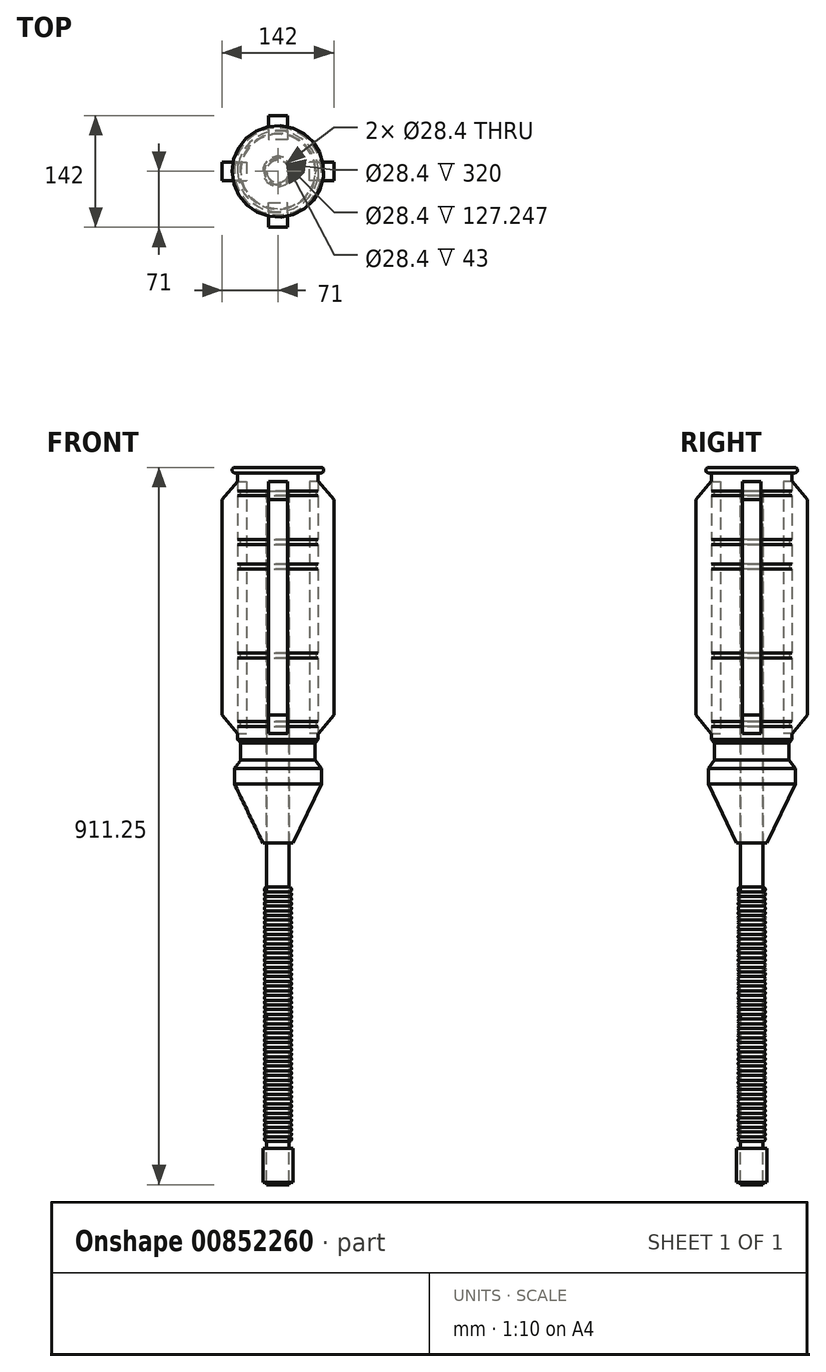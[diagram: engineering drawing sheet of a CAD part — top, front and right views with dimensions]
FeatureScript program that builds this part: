
annotation { "Feature Type Name" : "Feature", "Feature Type Description" : "" }
export const myFeature = defineFeature(function(context is Context, id is Id, definition is map)
    precondition{}
    {
        {
            var Q0;
            Q0=qCreatedBy(makeId("Front.planeOp"),FACE);
            var sketch = newSketch(context, id + "F0", { "sketchPlane" : qUnion([Q0])});
            skLineSegment(sketch, "E0", {"start": v(55.2, 58.28) * mm, "end": v(55.2, 78.28) * mm});
            skLineSegment(sketch, "E1", {"start": v(47.2, 88.53) * mm, "end": v(47.2, 110.53) * mm});
            skLineSegment(sketch, "E2", {"start": v(47.2, 110.53) * mm, "end": v(14.2, 110.53) * mm});
            skLineSegment(sketch, "E3", {"start": v(14.2, -16.72) * mm, "end": v(14.2, 110.53) * mm});
            skLineSegment(sketch, "E4", {"start": v(55.2, 78.28) * mm, "end": v(47.2, 88.53) * mm});
            skLineSegment(sketch, "E5", {"start": v(19.2, -16.72) * mm, "end": v(14.2, -16.72) * mm});
            skLineSegment(sketch, "E6", {"start": v(14.2, 110.53) * mm, "end": v(47.2, 110.53) * mm});
            skLineSegment(sketch, "E7", {"start": v(55.2, 58.28) * mm, "end": v(19.2, -16.72) * mm});
            skSolve(sketch);
        }
        {
            var Q0;
            Q0=qCreatedBy(makeId("Front.planeOp"),FACE);
            var sketch = newSketch(context, id + "F1", { "sketchPlane" : qUnion([Q0])});
            skLineSegment(sketch, "E8", {"start": v(0, 0) * mm, "end": v(0, 46.49) * mm});
            skSolve(sketch);
        }
        {
            var Q0;
            Q0 = qSketchRegion(id + "F0", true);
            var Q1;
            Q1=sQuery(id+"F1.wireOp",EDGE,"E8");
            revolve(context, id + "F2", {"surfaceOperationType" : NewSurfaceOperationType.NEW, "entities" : qUnion([Q0]), "axis" : qUnion([Q1]), "revolveType" : RevolveType.FULL});
        }
        {
            var Q0;
            Q0=qCreatedBy(makeId("Front.planeOp"),FACE);
            var sketch = newSketch(context, id + "F3", { "sketchPlane" : qUnion([Q0])});
            skLineSegment(sketch, "E9", {"start": v(51.2, 113.53) * mm, "end": v(51.2, 131.53) * mm});
            skLineSegment(sketch, "E10", {"start": v(54.74, 460.53) * mm, "end": v(14.2, 460.53) * mm});
            skLineSegment(sketch, "E11", {"start": v(51.2, 453.53) * mm, "end": v(54.7, 453.53) * mm});
            skLineSegment(sketch, "E12", {"start": v(58.2, 457.03) * mm, "end": v(58.2, 457.03) * mm});
            skLineSegment(sketch, "E13", {"start": v(54.7, 460.53) * mm, "end": v(54.74, 460.53) * mm});
            skPoint(sketch, "E14.visualSharp", {"position": v(58.2, 460.53) * mm});
            skArc(sketch, "E14.filletArc", {"start": v(58.2, 457.03) * mm, "mid": v(57.17, 459.5) * mm, "end": v(54.7, 460.53) * mm});
            skPoint(sketch, "E15.visualSharp", {"position": v(58.2, 453.53) * mm});
            skArc(sketch, "E15.filletArc", {"start": v(54.7, 453.53) * mm, "mid": v(57.17, 454.56) * mm, "end": v(58.2, 457.03) * mm});
            skLineSegment(sketch, "E16", {"start": v(51.2, 131.53) * mm, "end": v(48.2, 131.53) * mm});
            skLineSegment(sketch, "E17", {"start": v(48.2, 131.53) * mm, "end": v(48.2, 137.53) * mm});
            skLineSegment(sketch, "E18", {"start": v(48.2, 137.53) * mm, "end": v(51.2, 137.53) * mm});
            skLineSegment(sketch, "E19.trimOffspring", {"start": v(51.2, 137.53) * mm, "end": v(51.2, 218.53) * mm});
            skLineSegment(sketch, "E20", {"start": v(51.2, 218.53) * mm, "end": v(48.2, 218.53) * mm});
            skLineSegment(sketch, "E21", {"start": v(48.2, 218.53) * mm, "end": v(48.2, 224.53) * mm});
            skLineSegment(sketch, "E22", {"start": v(48.2, 224.53) * mm, "end": v(51.2, 224.53) * mm});
            skLineSegment(sketch, "E23", {"start": v(51.2, 331.53) * mm, "end": v(48.2, 331.53) * mm});
            skLineSegment(sketch, "E24", {"start": v(48.2, 331.53) * mm, "end": v(48.2, 337.53) * mm});
            skLineSegment(sketch, "E25", {"start": v(48.2, 337.53) * mm, "end": v(51.2, 337.53) * mm});
            skLineSegment(sketch, "E26", {"start": v(51.2, 362.53) * mm, "end": v(48.2, 362.53) * mm});
            skLineSegment(sketch, "E27", {"start": v(48.2, 362.53) * mm, "end": v(48.2, 368.53) * mm});
            skLineSegment(sketch, "E28", {"start": v(48.2, 368.53) * mm, "end": v(51.2, 368.53) * mm});
            skLineSegment(sketch, "E29", {"start": v(51.2, 424.53) * mm, "end": v(48.2, 424.53) * mm});
            skLineSegment(sketch, "E30", {"start": v(48.2, 424.53) * mm, "end": v(48.2, 430.53) * mm});
            skLineSegment(sketch, "E31", {"start": v(48.2, 430.53) * mm, "end": v(51.2, 430.53) * mm});
            skLineSegment(sketch, "E32.trimOffspring", {"start": v(51.2, 430.53) * mm, "end": v(51.2, 453.53) * mm});
            skLineSegment(sketch, "E33.trimOffspring", {"start": v(51.2, 368.53) * mm, "end": v(51.2, 424.53) * mm});
            skLineSegment(sketch, "E34.trimOffspring", {"start": v(51.2, 337.53) * mm, "end": v(51.2, 362.53) * mm});
            skLineSegment(sketch, "E35.trimOffspring", {"start": v(51.2, 224.53) * mm, "end": v(51.2, 331.53) * mm});
            skLineSegment(sketch, "E36", {"start": v(15.98, 110.53) * mm, "end": v(40.96, 110.53) * mm});
            skLineSegment(sketch, "E37", {"start": v(51.2, 112.1) * mm, "end": v(51.2, 113.53) * mm});
            skLineSegment(sketch, "E38", {"start": v(14.2, 110.53) * mm, "end": v(14.2, 430.53) * mm});
            skLineSegment(sketch, "E39", {"start": v(14.2, 110.53) * mm, "end": v(15.98, 110.53) * mm});
            skLineSegment(sketch, "E40", {"start": v(14.2, 460.53) * mm, "end": v(0, 460.53) * mm});
            skLineSegment(sketch, "E41", {"start": v(0, 460.53) * mm, "end": v(0, 430.53) * mm});
            skLineSegment(sketch, "E42", {"start": v(0, 430.53) * mm, "end": v(14.2, 430.53) * mm});
            skLineSegment(sketch, "E43", {"start": v(40.96, 110.53) * mm, "end": v(51.2, 110.53) * mm});
            skLineSegment(sketch, "E44", {"start": v(51.2, 110.53) * mm, "end": v(51.2, 112.1) * mm});
            skSolve(sketch);
        }
        {
            var Q0;
            Q0=qCreatedBy(makeId("Front.planeOp"),FACE);
            var sketch = newSketch(context, id + "F4", { "sketchPlane" : qUnion([Q0])});
            skLineSegment(sketch, "E45", {"start": v(0, 0) * mm, "end": v(0, 511.65) * mm});
            skSolve(sketch);
        }
        {
            var Q0;
            Q0 = qSketchRegion(id + "F3", true);
            var Q1;
            Q1=sQuery(id+"F4.wireOp",EDGE,"E45");
            revolve(context, id + "F5", {"surfaceOperationType" : NewSurfaceOperationType.NEW, "entities" : qUnion([Q0]), "axis" : qUnion([Q1]), "revolveType" : RevolveType.FULL});
        }
        {
            var Q0;
            Q0=qCreatedBy(makeId("Front.planeOp"),FACE);
            var sketch = newSketch(context, id + "F6", { "sketchPlane" : qUnion([Q0])});
            skLineSegment(sketch, "E46", {"start": v(0, 122.6) * mm, "end": v(12, 122.6) * mm});
            skLineSegment(sketch, "E47", {"start": v(0, 122.6) * mm, "end": v(-12, 122.6) * mm});
            skLineSegment(sketch, "E48", {"start": v(-12, 122.6) * mm, "end": v(-12, 442.6) * mm});
            skLineSegment(sketch, "E49", {"start": v(-12, 442.6) * mm, "end": v(12, 442.6) * mm});
            skLineSegment(sketch, "E50", {"start": v(12, 442.6) * mm, "end": v(12, 122.6) * mm});
            skSolve(sketch);
        }
        {
            var Q0;
            Q0 = qSketchRegion(id + "F6", true);
            extrude(context, id + "F7", {"entities" : qUnion([Q0]), "depth" : 71 * mm, "offsetDistance" : 25 * mm, "hasSecondDirection" : true, "secondDirectionOppositeDirection" : false, "secondDirectionDepth" : 40 * mm});
        }
        {
            var Q0;
            Q0=qCreatedBy(makeId("Front.planeOp"),FACE);
            var sketch = newSketch(context, id + "F8", { "sketchPlane" : qUnion([Q0])});
            skLineSegment(sketch, "E51", {"start": v(0, 0) * mm, "end": v(0, 45.37) * mm});
            skSolve(sketch);
        }
        {
            var Q0;
            Q0=makeQuery(id+"F7.opExtrude","SWEPT_FACE",FACE,{"disambiguationData":[OSD([sQuery(id+"F6.wireOp",EDGE,"E50")])]});
            var sketch = newSketch(context, id + "F9", { "sketchPlane" : qUnion([Q0])});
            skLineSegment(sketch, "E52", {"start": v(-51.62, 442.6) * mm, "end": v(-71, 419.5) * mm});
            skLineSegment(sketch, "E53", {"start": v(-71, 419.5) * mm, "end": v(-71, 442.6) * mm});
            skLineSegment(sketch, "E54", {"start": v(-71, 442.6) * mm, "end": v(-51.62, 442.6) * mm});
            skLineSegment(sketch, "E55", {"start": v(-71, 145.7) * mm, "end": v(-51.62, 122.6) * mm});
            skLineSegment(sketch, "E56", {"start": v(-51.62, 122.6) * mm, "end": v(-71, 122.6) * mm});
            skLineSegment(sketch, "E57", {"start": v(-71, 122.6) * mm, "end": v(-71, 145.7) * mm});
            skLineSegment(sketch, "E58", {"start": v(-51.2, 430.53) * mm, "end": v(-51.2, 453.53) * mm});
            skSolve(sketch);
        }
        {
            var Q0;
            Q0=makeQuery(id+"F9.imprint","IMPRINT",FACE,{"disambiguationData":[TD([[makeQuery(id+"F9.imprint","IMPRINT",EDGE,{"derivedFrom":sQuery(id+"F9.wireOp",EDGE,"E52")}),-1.0]])]});
            var Q1;
            Q1=makeQuery(id+"F9.imprint","IMPRINT",FACE,{"disambiguationData":[TD([[makeQuery(id+"F9.imprint","IMPRINT",EDGE,{"derivedFrom":sQuery(id+"F9.wireOp",EDGE,"E55")}),-1.0]])]});
            extrude(context, id + "F10", {"entities" : qUnion([Q0, Q1]), "operationType" : NewBodyOperationType.REMOVE, "endBound" : BoundingType.UP_TO_NEXT, "oppositeDirection" : true, "depth" : 25 * mm, "offsetDistance" : 25 * mm});
        }
        {
            var Q0;
            Q0=makeQuery(id+"F7.opExtrude","SWEPT_BODY",BODY,{"disambiguationData":[OSD([sQuery(id+"F6.wireOp",EDGE,"E46"),sQuery(id+"F6.wireOp",EDGE,"E47"),sQuery(id+"F6.wireOp",EDGE,"E48"),sQuery(id+"F6.wireOp",EDGE,"E49"),sQuery(id+"F6.wireOp",EDGE,"E50")])]});
            var Q1;
            Q1=sQuery(id+"F8.wireOp",EDGE,"E51");
            circularPattern(context, id + "F11", {"entities" : qUnion([Q0]), "axis" : qUnion([Q1]), "angle" : 360 * degree, "instanceCount" : 4, "equalSpace" : true});
        }
        {
            var Q0;
            Q0=makeQuery(id+"F2.opRevolve","SWEPT_FACE",FACE,{"disambiguationData":[OSD([sQuery(id+"F0.wireOp",EDGE,"E5")])]});
            var sketch = newSketch(context, id + "F12", { "sketchPlane" : qUnion([Q0])});
            skCircle(sketch, "E59", {"center": v(0, 0) * mm, "radius": 14.23 * mm});
            skSolve(sketch);
        }
        {
            var Q0;
            Q0=makeQuery(id+"F12.imprint","IMPRINT",FACE,{"disambiguationData":[TD([[makeQuery(id+"F12.imprint","IMPRINT",EDGE,{"derivedFrom":makeQuery(id+"F2.opRevolve","SWEPT_EDGE",EDGE,{"disambiguationData":[OSD([sQuery(id+"F0.wireOp",EDGE,"E3"),sQuery(id+"F0.wireOp",EDGE,"E5")])]})}),1.0]])]});
            extrude(context, id + "F13", {"entities" : qUnion([Q0]), "depth" : 434 * mm, "offsetDistance" : 25 * mm, "hasSecondDirection" : true, "secondDirectionOppositeDirection" : true, "secondDirectionDepth" : 447.2 * mm});
        }
        {
            var Q0;
            Q0=makeQuery(id+"F13.opExtrude","CAP_FACE",FACE,{"disambiguationData":[OSD([sQuery(id+"F0.wireOp",EDGE,"E3"),sQuery(id+"F0.wireOp",EDGE,"E5")])],"isStart":false});
            var sketch = newSketch(context, id + "F14", { "sketchPlane" : qUnion([Q0])});
            skCircle(sketch, "E60", {"center": v(0, 0) * mm, "radius": 14.2 * mm});
            skCircle(sketch, "E61", {"center": v(0, 0) * mm, "radius": 19.2 * mm});
            skSolve(sketch);
        }
        {
            var Q0;
            Q0=makeQuery(id+"F14.imprint","IMPRINT",FACE,{"disambiguationData":[TD([[makeQuery(id+"F14.imprint","IMPRINT",EDGE,{"derivedFrom":sQuery(id+"F14.wireOp",EDGE,"E60")}),-1.0]])]});
            extrude(context, id + "F15", {"entities" : qUnion([Q0]), "oppositeDirection" : true, "depth" : 46 * mm, "offsetDistance" : 25 * mm, "hasSecondDirection" : true, "secondDirectionOppositeDirection" : true, "secondDirectionDepth" : 3 * mm});
        }
        {
            var Q0;
            Q0=qCreatedBy(makeId("Right.planeOp"),FACE);
            var sketch = newSketch(context, id + "F16", { "sketchPlane" : qUnion([Q0])});
            skArc(sketch, "E62", {"start": v(14.2, -78.82) * mm, "mid": v(17.2, -75.82) * mm, "end": v(14.2, -72.82) * mm});
            skLineSegment(sketch, "E63", {"start": v(14.2, -72.82) * mm, "end": v(14.2, -78.82) * mm});
            skArc(sketch, "E64.1.0.0", {"start": v(14.2, -84.8) * mm, "mid": v(17.2, -81.8) * mm, "end": v(14.2, -78.8) * mm});
            skLineSegment(sketch, "E64.1.0.1", {"start": v(14.2, -78.8) * mm, "end": v(14.2, -84.8) * mm});
            skArc(sketch, "E64.2.0.0", {"start": v(14.2, -90.78) * mm, "mid": v(17.2, -87.78) * mm, "end": v(14.2, -84.78) * mm});
            skLineSegment(sketch, "E64.2.0.1", {"start": v(14.2, -84.78) * mm, "end": v(14.2, -90.78) * mm});
            skArc(sketch, "E64.3.0.0", {"start": v(14.2, -96.76) * mm, "mid": v(17.2, -93.76) * mm, "end": v(14.2, -90.76) * mm});
            skLineSegment(sketch, "E64.3.0.1", {"start": v(14.2, -90.76) * mm, "end": v(14.2, -96.76) * mm});
            skArc(sketch, "E64.4.0.0", {"start": v(14.2, -102.74) * mm, "mid": v(17.2, -99.74) * mm, "end": v(14.2, -96.74) * mm});
            skLineSegment(sketch, "E64.4.0.1", {"start": v(14.2, -96.74) * mm, "end": v(14.2, -102.74) * mm});
            skArc(sketch, "E64.5.0.0", {"start": v(14.2, -108.72) * mm, "mid": v(17.2, -105.72) * mm, "end": v(14.2, -102.72) * mm});
            skLineSegment(sketch, "E64.5.0.1", {"start": v(14.2, -102.72) * mm, "end": v(14.2, -108.72) * mm});
            skArc(sketch, "E64.6.0.0", {"start": v(14.2, -114.7) * mm, "mid": v(17.2, -111.7) * mm, "end": v(14.2, -108.7) * mm});
            skLineSegment(sketch, "E64.6.0.1", {"start": v(14.2, -108.7) * mm, "end": v(14.2, -114.7) * mm});
            skArc(sketch, "E64.7.0.0", {"start": v(14.2, -120.68) * mm, "mid": v(17.2, -117.68) * mm, "end": v(14.2, -114.68) * mm});
            skLineSegment(sketch, "E64.7.0.1", {"start": v(14.2, -114.68) * mm, "end": v(14.2, -120.68) * mm});
            skArc(sketch, "E64.8.0.0", {"start": v(14.2, -126.66) * mm, "mid": v(17.2, -123.66) * mm, "end": v(14.2, -120.66) * mm});
            skLineSegment(sketch, "E64.8.0.1", {"start": v(14.2, -120.66) * mm, "end": v(14.2, -126.66) * mm});
            skArc(sketch, "E64.9.0.0", {"start": v(14.2, -132.64) * mm, "mid": v(17.2, -129.64) * mm, "end": v(14.2, -126.64) * mm});
            skLineSegment(sketch, "E64.9.0.1", {"start": v(14.2, -126.64) * mm, "end": v(14.2, -132.64) * mm});
            skArc(sketch, "E64.10.0.0", {"start": v(14.2, -138.62) * mm, "mid": v(17.2, -135.62) * mm, "end": v(14.2, -132.62) * mm});
            skLineSegment(sketch, "E64.10.0.1", {"start": v(14.2, -132.62) * mm, "end": v(14.2, -138.62) * mm});
            skArc(sketch, "E64.11.0.0", {"start": v(14.2, -144.6) * mm, "mid": v(17.2, -141.6) * mm, "end": v(14.2, -138.6) * mm});
            skLineSegment(sketch, "E64.11.0.1", {"start": v(14.2, -138.6) * mm, "end": v(14.2, -144.6) * mm});
            skArc(sketch, "E64.12.0.0", {"start": v(14.2, -150.58) * mm, "mid": v(17.2, -147.58) * mm, "end": v(14.2, -144.58) * mm});
            skLineSegment(sketch, "E64.12.0.1", {"start": v(14.2, -144.58) * mm, "end": v(14.2, -150.58) * mm});
            skArc(sketch, "E64.13.0.0", {"start": v(14.2, -156.56) * mm, "mid": v(17.2, -153.56) * mm, "end": v(14.2, -150.56) * mm});
            skLineSegment(sketch, "E64.13.0.1", {"start": v(14.2, -150.56) * mm, "end": v(14.2, -156.56) * mm});
            skArc(sketch, "E64.14.0.0", {"start": v(14.2, -162.54) * mm, "mid": v(17.2, -159.54) * mm, "end": v(14.2, -156.54) * mm});
            skLineSegment(sketch, "E64.14.0.1", {"start": v(14.2, -156.54) * mm, "end": v(14.2, -162.54) * mm});
            skArc(sketch, "E64.15.0.0", {"start": v(14.2, -168.52) * mm, "mid": v(17.2, -165.52) * mm, "end": v(14.2, -162.52) * mm});
            skLineSegment(sketch, "E64.15.0.1", {"start": v(14.2, -162.52) * mm, "end": v(14.2, -168.52) * mm});
            skArc(sketch, "E64.16.0.0", {"start": v(14.2, -174.5) * mm, "mid": v(17.2, -171.5) * mm, "end": v(14.2, -168.5) * mm});
            skLineSegment(sketch, "E64.16.0.1", {"start": v(14.2, -168.5) * mm, "end": v(14.2, -174.5) * mm});
            skArc(sketch, "E64.17.0.0", {"start": v(14.2, -180.48) * mm, "mid": v(17.2, -177.48) * mm, "end": v(14.2, -174.48) * mm});
            skLineSegment(sketch, "E64.17.0.1", {"start": v(14.2, -174.48) * mm, "end": v(14.2, -180.48) * mm});
            skArc(sketch, "E64.18.0.0", {"start": v(14.2, -186.46) * mm, "mid": v(17.2, -183.46) * mm, "end": v(14.2, -180.46) * mm});
            skLineSegment(sketch, "E64.18.0.1", {"start": v(14.2, -180.46) * mm, "end": v(14.2, -186.46) * mm});
            skArc(sketch, "E64.19.0.0", {"start": v(14.2, -192.44) * mm, "mid": v(17.2, -189.44) * mm, "end": v(14.2, -186.44) * mm});
            skLineSegment(sketch, "E64.19.0.1", {"start": v(14.2, -186.44) * mm, "end": v(14.2, -192.44) * mm});
            skArc(sketch, "E64.20.0.0", {"start": v(14.2, -198.42) * mm, "mid": v(17.2, -195.42) * mm, "end": v(14.2, -192.42) * mm});
            skLineSegment(sketch, "E64.20.0.1", {"start": v(14.2, -192.42) * mm, "end": v(14.2, -198.42) * mm});
            skArc(sketch, "E64.21.0.0", {"start": v(14.2, -204.4) * mm, "mid": v(17.2, -201.4) * mm, "end": v(14.2, -198.4) * mm});
            skLineSegment(sketch, "E64.21.0.1", {"start": v(14.2, -198.4) * mm, "end": v(14.2, -204.4) * mm});
            skArc(sketch, "E64.22.0.0", {"start": v(14.2, -210.38) * mm, "mid": v(17.2, -207.38) * mm, "end": v(14.2, -204.38) * mm});
            skLineSegment(sketch, "E64.22.0.1", {"start": v(14.2, -204.38) * mm, "end": v(14.2, -210.38) * mm});
            skArc(sketch, "E64.23.0.0", {"start": v(14.2, -216.36) * mm, "mid": v(17.2, -213.36) * mm, "end": v(14.2, -210.36) * mm});
            skLineSegment(sketch, "E64.23.0.1", {"start": v(14.2, -210.36) * mm, "end": v(14.2, -216.36) * mm});
            skArc(sketch, "E64.24.0.0", {"start": v(14.2, -222.34) * mm, "mid": v(17.2, -219.34) * mm, "end": v(14.2, -216.34) * mm});
            skLineSegment(sketch, "E64.24.0.1", {"start": v(14.2, -216.34) * mm, "end": v(14.2, -222.34) * mm});
            skArc(sketch, "E64.25.0.0", {"start": v(14.2, -228.32) * mm, "mid": v(17.2, -225.32) * mm, "end": v(14.2, -222.32) * mm});
            skLineSegment(sketch, "E64.25.0.1", {"start": v(14.2, -222.32) * mm, "end": v(14.2, -228.32) * mm});
            skArc(sketch, "E64.26.0.0", {"start": v(14.2, -234.3) * mm, "mid": v(17.2, -231.3) * mm, "end": v(14.2, -228.3) * mm});
            skLineSegment(sketch, "E64.26.0.1", {"start": v(14.2, -228.3) * mm, "end": v(14.2, -234.3) * mm});
            skLineSegment(sketch, "E64.direction1", {"start": v(14.2, -78.82) * mm, "end": v(14.2, -84.8) * mm, "construction": true});
            skLineSegment(sketch, "E65.0", {"start": v(19.2, -16.72) * mm, "end": v(-19.2, -16.72) * mm});
            skLineSegment(sketch, "E66.0", {"start": v(19.2, -404.72) * mm, "end": v(-19.2, -404.72) * mm});
            skSolve(sketch);
        }
        {
            var Q0;
            Q0=qCreatedBy(makeId("Right.planeOp"),FACE);
            var sketch = newSketch(context, id + "F17", { "sketchPlane" : qUnion([Q0])});
            skLineSegment(sketch, "E67", {"start": v(0, 0) * mm, "end": v(0, -41.27) * mm});
            skSolve(sketch);
        }
        {
            var Q0;
            Q0 = qSketchRegion(id + "F16", true);
            var Q1;
            Q1=sQuery(id+"F17.wireOp",EDGE,"E67");
            revolve(context, id + "F18", {"surfaceOperationType" : NewSurfaceOperationType.NEW, "entities" : qUnion([Q0]), "axis" : qUnion([Q1]), "revolveType" : RevolveType.FULL});
        }
        {
            var Q0;
            Q0=makeQuery(id+"F5.opRevolve","SWEPT_EDGE",EDGE,{"disambiguationData":[OSD([sQuery(id+"F3.wireOp",EDGE,"E43"),sQuery(id+"F3.wireOp",EDGE,"E44")])]});
            chamfer(context, id + "F19", {"entities" : qUnion([Q0]), "chamferType" : ChamferType.OFFSET_ANGLE, "width" : 4 * mm, "oppositeDirection" : false, "angle" : 45 * degree, "tangentPropagation" : true});
        }
        {
            var Q0;
            Q0=makeQuery(id+"F2.opRevolve","SWEPT_FACE",FACE,{"disambiguationData":[OSD([sQuery(id+"F0.wireOp",EDGE,"E5")])]});
            cPlane(context, id + "F20", {"entities" : qUnion([Q0]), "cplaneType" : CPlaneType.OFFSET, "offset" : 217.58 * mm, "width" : 150 * mm, "height" : 150 * mm});
        }
        {
            var Q0;
            Q0=makeQuery(id+"F18.opRevolve","SWEPT_BODY",BODY,{"disambiguationData":[OSD([sQuery(id+"F16.wireOp",EDGE,"E62"),sQuery(id+"F16.wireOp",EDGE,"E63"),sQuery(id+"F16.wireOp",EDGE,"E64.1.0.0"),sQuery(id+"F16.wireOp",EDGE,"E64.1.0.1"),sQuery(id+"F16.wireOp",EDGE,"E64.2.0.0"),sQuery(id+"F16.wireOp",EDGE,"E64.2.0.1"),sQuery(id+"F16.wireOp",EDGE,"E64.3.0.0"),sQuery(id+"F16.wireOp",EDGE,"E64.3.0.1"),sQuery(id+"F16.wireOp",EDGE,"E64.4.0.0"),sQuery(id+"F16.wireOp",EDGE,"E64.4.0.1"),sQuery(id+"F16.wireOp",EDGE,"E64.5.0.0"),sQuery(id+"F16.wireOp",EDGE,"E64.5.0.1"),sQuery(id+"F16.wireOp",EDGE,"E64.6.0.0"),sQuery(id+"F16.wireOp",EDGE,"E64.6.0.1"),sQuery(id+"F16.wireOp",EDGE,"E64.7.0.0"),sQuery(id+"F16.wireOp",EDGE,"E64.7.0.1"),sQuery(id+"F16.wireOp",EDGE,"E64.8.0.0"),sQuery(id+"F16.wireOp",EDGE,"E64.8.0.1"),sQuery(id+"F16.wireOp",EDGE,"E64.9.0.0"),sQuery(id+"F16.wireOp",EDGE,"E64.9.0.1"),sQuery(id+"F16.wireOp",EDGE,"E64.10.0.0"),sQuery(id+"F16.wireOp",EDGE,"E64.10.0.1"),sQuery(id+"F16.wireOp",EDGE,"E64.11.0.0"),sQuery(id+"F16.wireOp",EDGE,"E64.11.0.1"),sQuery(id+"F16.wireOp",EDGE,"E64.12.0.0"),sQuery(id+"F16.wireOp",EDGE,"E64.12.0.1"),sQuery(id+"F16.wireOp",EDGE,"E64.13.0.0"),sQuery(id+"F16.wireOp",EDGE,"E64.13.0.1"),sQuery(id+"F16.wireOp",EDGE,"E64.14.0.0"),sQuery(id+"F16.wireOp",EDGE,"E64.14.0.1"),sQuery(id+"F16.wireOp",EDGE,"E64.15.0.0"),sQuery(id+"F16.wireOp",EDGE,"E64.15.0.1"),sQuery(id+"F16.wireOp",EDGE,"E64.16.0.0"),sQuery(id+"F16.wireOp",EDGE,"E64.16.0.1"),sQuery(id+"F16.wireOp",EDGE,"E64.17.0.0"),sQuery(id+"F16.wireOp",EDGE,"E64.17.0.1"),sQuery(id+"F16.wireOp",EDGE,"E64.18.0.0"),sQuery(id+"F16.wireOp",EDGE,"E64.18.0.1"),sQuery(id+"F16.wireOp",EDGE,"E64.19.0.0"),sQuery(id+"F16.wireOp",EDGE,"E64.19.0.1"),sQuery(id+"F16.wireOp",EDGE,"E64.20.0.0"),sQuery(id+"F16.wireOp",EDGE,"E64.20.0.1"),sQuery(id+"F16.wireOp",EDGE,"E64.21.0.0"),sQuery(id+"F16.wireOp",EDGE,"E64.21.0.1"),sQuery(id+"F16.wireOp",EDGE,"E64.22.0.0"),sQuery(id+"F16.wireOp",EDGE,"E64.22.0.1"),sQuery(id+"F16.wireOp",EDGE,"E64.23.0.0"),sQuery(id+"F16.wireOp",EDGE,"E64.23.0.1"),sQuery(id+"F16.wireOp",EDGE,"E64.24.0.0"),sQuery(id+"F16.wireOp",EDGE,"E64.24.0.1"),sQuery(id+"F16.wireOp",EDGE,"E64.25.0.0"),sQuery(id+"F16.wireOp",EDGE,"E64.25.0.1"),sQuery(id+"F16.wireOp",EDGE,"E64.26.0.0"),sQuery(id+"F16.wireOp",EDGE,"E64.26.0.1"),sQuery(id+"F16.wireOp",EDGE,"E64.27.0.0"),sQuery(id+"F16.wireOp",EDGE,"E64.27.0.1")])]});
            var Q1;
            Q1=qCreatedBy(id+"F20.planeOp",FACE);
            mirror(context, id + "F21", {"entities" : qUnion([Q0]), "mirrorPlane" : qUnion([Q1])});
        }
    });
